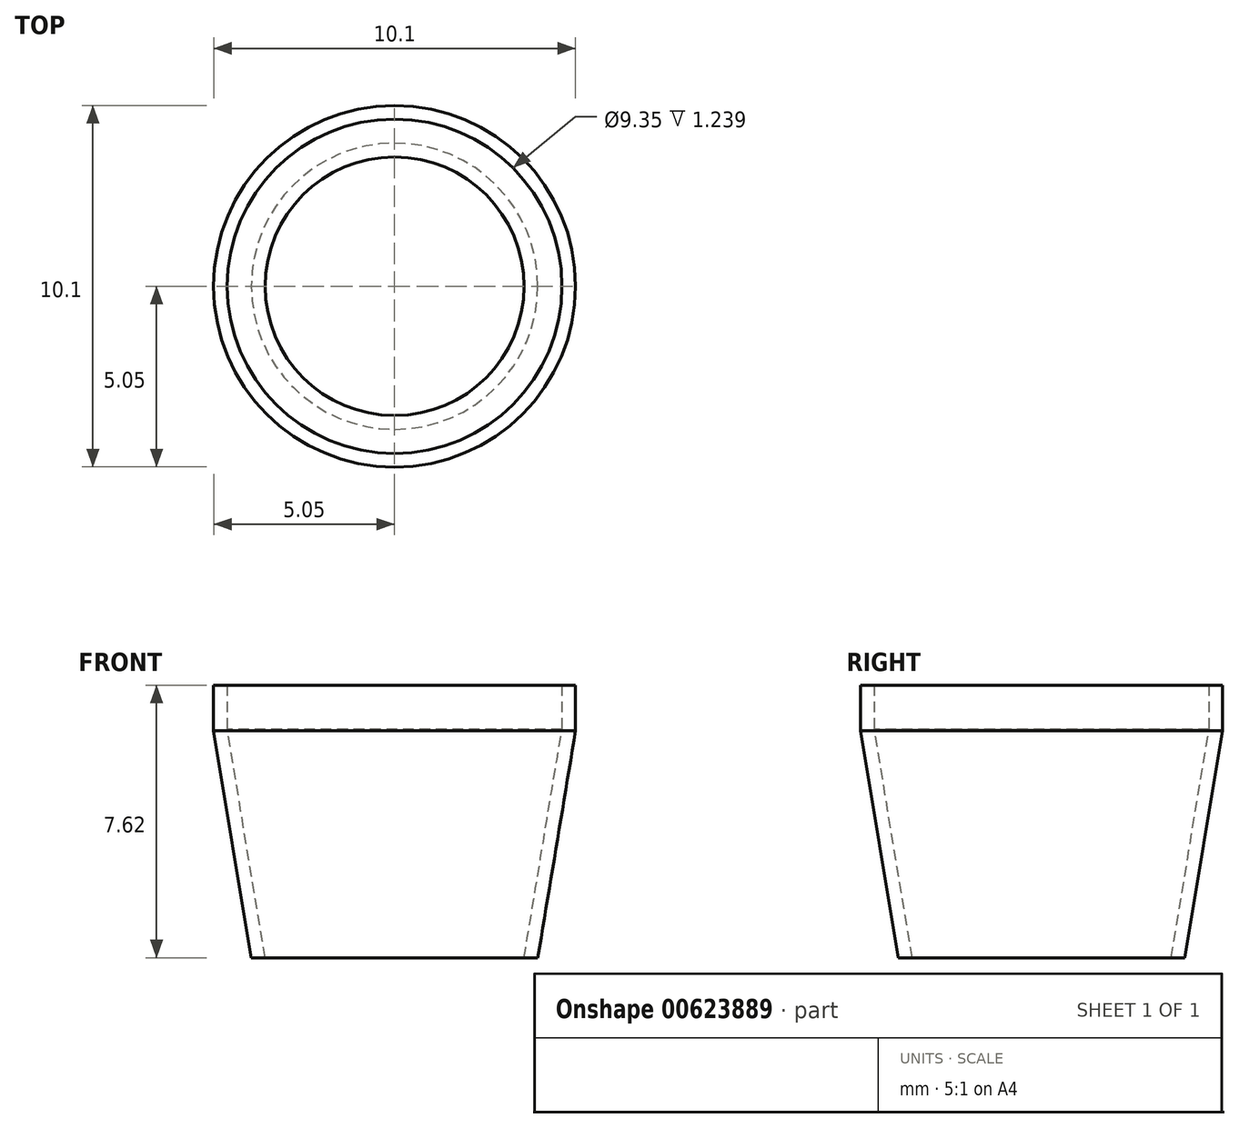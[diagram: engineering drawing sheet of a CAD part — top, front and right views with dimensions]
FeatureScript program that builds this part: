
annotation { "Feature Type Name" : "Feature", "Feature Type Description" : "" }
export const myFeature = defineFeature(function(context is Context, id is Id, definition is map)
    precondition{}
    {
        {
            var Q0;
            Q0=qCreatedBy(makeId("Top.planeOp"),FACE);
            var sketch = newSketch(context, id + "F0", { "sketchPlane" : qUnion([Q0])});
            skCircle(sketch, "E0", {"center": v(0, 0) * mm, "radius": 4 * mm});
            skSolve(sketch);
        }
        {
            var Q0;
            Q0=qCreatedBy(makeId("Top.planeOp"),FACE);
            cPlane(context, id + "F1", {"entities" : qUnion([Q0]), "cplaneType" : CPlaneType.OFFSET, "offset" : 6.35 * mm, "width" : 152.4 * mm, "height" : 152.4 * mm});
        }
        {
            var Q0;
            Q0=qCreatedBy(id+"F1.planeOp",FACE);
            var sketch = newSketch(context, id + "F2", { "sketchPlane" : qUnion([Q0])});
            skCircle(sketch, "E1", {"center": v(0, 0) * mm, "radius": 5.05 * mm});
            skSolve(sketch);
        }
        {
            var Q0;
            Q0=makeQuery(id+"F2.imprint","IMPRINT",FACE,{"disambiguationData":[TD([[makeQuery(id+"F2.imprint","IMPRINT",EDGE,{"derivedFrom":sQuery(id+"F2.wireOp",EDGE,"E1")}),1.0]])]});
            extrude(context, id + "F3", {"entities" : qUnion([Q0]), "depth" : 1.27 * mm, "offsetDistance" : 25.4 * mm});
        }
        {
            var Q1;
            Q1=makeQuery(id+"F0.imprint","IMPRINT",FACE,{"disambiguationData":[TD([[makeQuery(id+"F0.imprint","IMPRINT",EDGE,{"derivedFrom":sQuery(id+"F0.wireOp",EDGE,"E0")}),1.0]])]});
            var Q2;
            Q2=makeQuery(id+"F3.opExtrude","CAP_FACE",FACE,{"disambiguationData":[OSD([sQuery(id+"F2.wireOp",EDGE,"E1")])],"isStart":true});
            loft(context, id + "F4", {"operationType" : NewBodyOperationType.ADD, "sheetProfilesArray" : [{ "sheetProfileEntities" : qUnion([Q1]) }, { "sheetProfileEntities" : qUnion([Q2]) }]});
        }
        {
            var Q0;
            Q0=makeQuery(id+"F4.opLoft","CAP_FACE",FACE,{"disambiguationData":[OSD([makeQuery(id+"F0.imprint","IMPRINT",FACE,{"disambiguationData":[TD([[makeQuery(id+"F0.imprint","IMPRINT",EDGE,{"derivedFrom":sQuery(id+"F0.wireOp",EDGE,"E0")}),1.0]])]})])],"isStart":true});
            shell(context, id + "F5", {"entities" : qUnion([Q0]), "thickness" : 0.38 * mm});
        }
        {
            var Q0;
            {var subQ0=sQuery(id+"F2.wireOp",EDGE,"E1");Q0=makeQuery(id+"F5.opShell","OFFSET_FACE",FACE,{"disambiguationData":[OSD([subQ0]),TDD([makeQuery(id+"F3.opExtrude","CAP_FACE",FACE,{"disambiguationData":[OSD([subQ0])],"isStart":false})])]});}
            var Q1;
            Q1=makeQuery(id+"F3.opExtrude","CAP_FACE",FACE,{"disambiguationData":[OSD([sQuery(id+"F2.wireOp",EDGE,"E1")])],"isStart":false});
            shell(context, id + "F6", {"entities" : qUnion([Q0, Q1]), "thickness" : 0.38 * mm});
        }
    });
